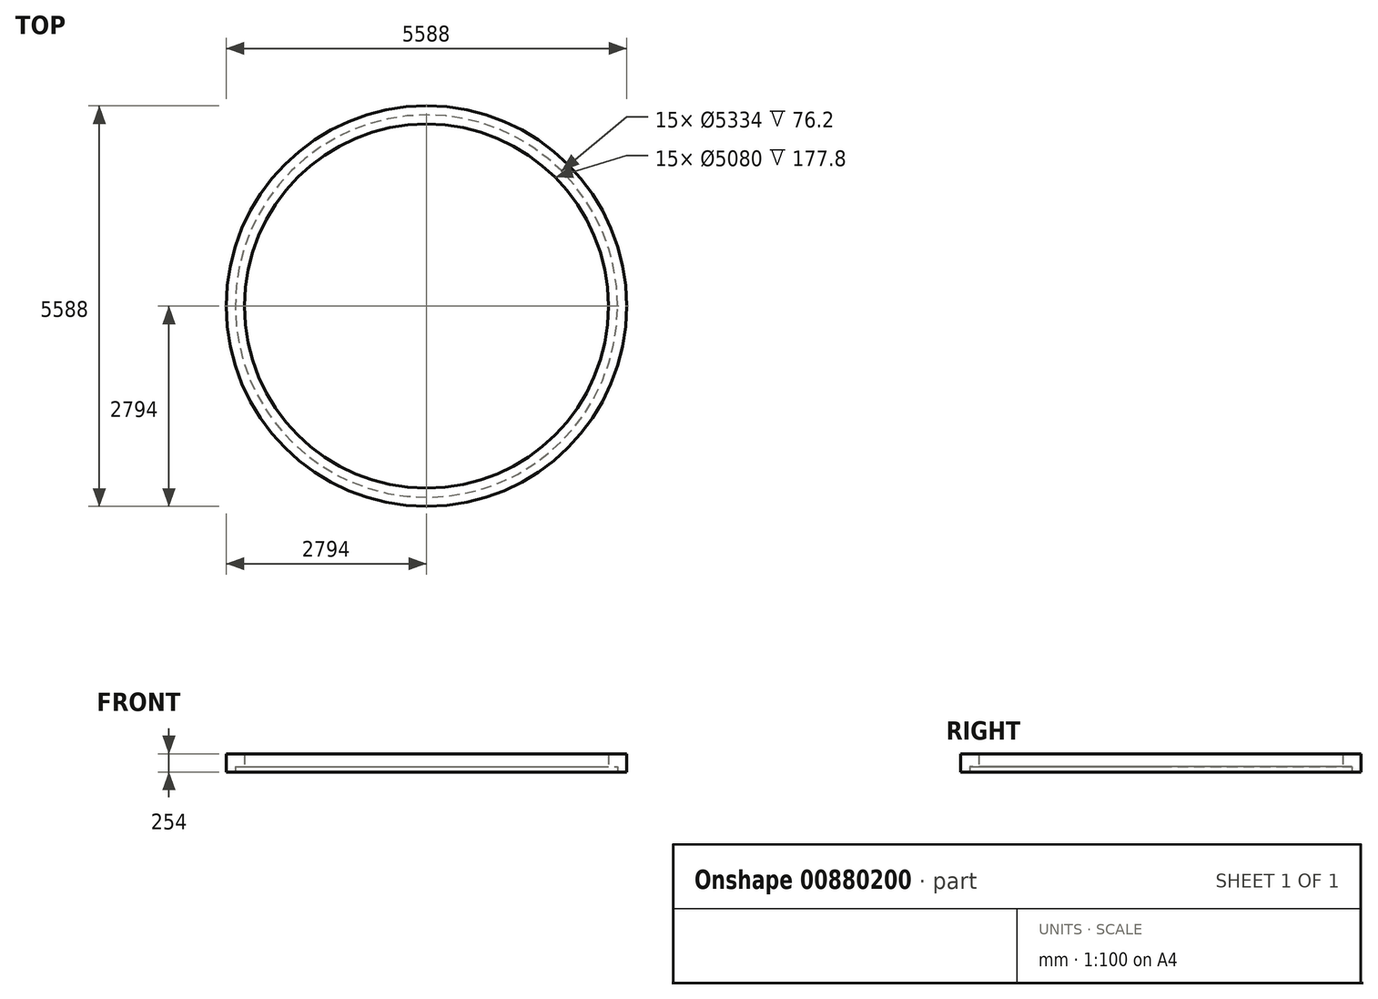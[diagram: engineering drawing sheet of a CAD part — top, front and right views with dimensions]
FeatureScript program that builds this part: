
annotation { "Feature Type Name" : "Feature", "Feature Type Description" : "" }
export const myFeature = defineFeature(function(context is Context, id is Id, definition is map)
    precondition{}
    {
        {
            var Q0;
            Q0=qCreatedBy(makeId("Front.planeOp"),FACE);
            var sketch = newSketch(context, id + "F0", { "sketchPlane" : qUnion([Q0])});
            skLineSegment(sketch, "E0", {"start": v(-2794, 0) * mm, "end": v(-2794, 254) * mm});
            skLineSegment(sketch, "E1", {"start": v(-2794, 254) * mm, "end": v(-2540, 254) * mm});
            skLineSegment(sketch, "E2", {"start": v(-2540, 254) * mm, "end": v(-2540, 0) * mm});
            skLineSegment(sketch, "E3", {"start": v(-2540, 0) * mm, "end": v(-2794, 0) * mm});
            skLineSegment(sketch, "E4", {"start": v(0, 0) * mm, "end": v(0, 517.88) * mm});
            skLineSegment(sketch, "E5", {"start": v(-2540, 76.2) * mm, "end": v(-2667, 76.2) * mm});
            skLineSegment(sketch, "E6", {"start": v(-2667, 76.2) * mm, "end": v(-2667, 0) * mm});
            skSolve(sketch);
        }
        {
            var Q0;
            Q0=makeQuery(id+"F0.imprint","IMPRINT",FACE,{"disambiguationData":[TD([[makeQuery(id+"F0.imprint","IMPRINT",EDGE,{"derivedFrom":sQuery(id+"F0.wireOp",EDGE,"E0")}),-1.0]])]});
            var Q1;
            Q1=sQuery(id+"F0.wireOp",EDGE,"E4");
            revolve(context, id + "F1", {"surfaceOperationType" : NewSurfaceOperationType.NEW, "entities" : qUnion([Q0]), "axis" : qUnion([Q1]), "revolveType" : RevolveType.FULL});
        }
    });
